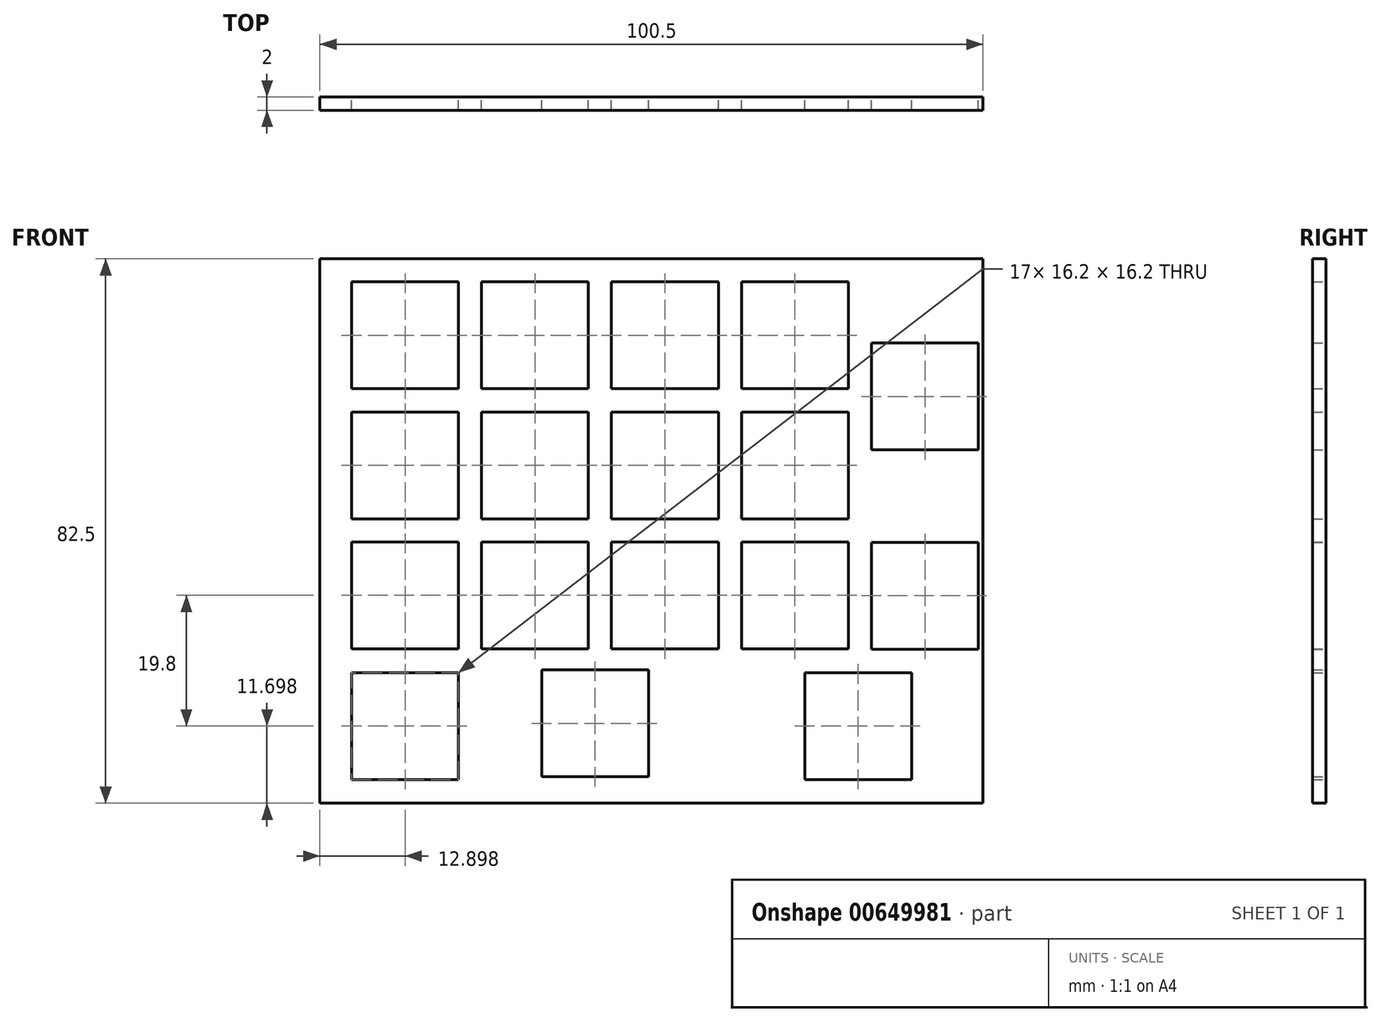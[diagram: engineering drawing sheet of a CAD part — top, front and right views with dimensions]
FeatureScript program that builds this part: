
annotation { "Feature Type Name" : "Feature", "Feature Type Description" : "" }
export const myFeature = defineFeature(function(context is Context, id is Id, definition is map)
    precondition{}
    {
        {
            var Q0;
            Q0=qCreatedBy(makeId("Front.planeOp"),FACE);
            var sketch = newSketch(context, id + "F0", { "sketchPlane" : qUnion([Q0])});
            skLineSegment(sketch, "E0.bottom", {"start": v(-117.36, -39.18) * mm, "end": v(-16.86, -39.18) * mm});
            skLineSegment(sketch, "E0.top", {"start": v(-117.36, 43.32) * mm, "end": v(-16.86, 43.32) * mm});
            skLineSegment(sketch, "E0.left", {"start": v(-117.36, -39.18) * mm, "end": v(-117.36, 43.32) * mm});
            skLineSegment(sketch, "E0.right", {"start": v(-16.86, -39.18) * mm, "end": v(-16.86, 43.32) * mm});
            skPoint(sketch, "E0.middle", {"position": v(-67.11, 2.07) * mm});
            skSolve(sketch);
        }
        {
            var Q0;
            Q0=makeQuery(id+"F0.imprint","IMPRINT",FACE,{"disambiguationData":[TD([[makeQuery(id+"F0.imprint","IMPRINT",EDGE,{"derivedFrom":sQuery(id+"F0.wireOp",EDGE,"E0.bottom")}),1.0]])]});
            extrude(context, id + "F1", {"entities" : qUnion([Q0]), "depth" : 2 * mm, "offsetDistance" : 25 * mm});
        }
        {
            var Q0;
            Q0=qCreatedBy(makeId("Front.planeOp"),FACE);
            var sketch = newSketch(context, id + "F2", { "sketchPlane" : qUnion([Q0])});
            skLineSegment(sketch, "E1.bottom", {"start": v(-96.36, 23.62) * mm, "end": v(-112.56, 23.62) * mm});
            skLineSegment(sketch, "E1.top", {"start": v(-96.36, 39.82) * mm, "end": v(-112.56, 39.82) * mm});
            skLineSegment(sketch, "E1.left", {"start": v(-96.36, 23.62) * mm, "end": v(-96.36, 39.82) * mm});
            skLineSegment(sketch, "E1.right", {"start": v(-112.56, 23.62) * mm, "end": v(-112.56, 39.82) * mm});
            skPoint(sketch, "E1.middle", {"position": v(-104.46, 31.72) * mm});
            skLineSegment(sketch, "E2.bottom", {"start": v(-96.36, 3.92) * mm, "end": v(-112.56, 3.92) * mm});
            skLineSegment(sketch, "E2.top", {"start": v(-96.36, 20.12) * mm, "end": v(-112.56, 20.12) * mm});
            skLineSegment(sketch, "E2.left", {"start": v(-96.36, 3.92) * mm, "end": v(-96.36, 20.12) * mm});
            skLineSegment(sketch, "E2.right", {"start": v(-112.56, 3.92) * mm, "end": v(-112.56, 20.12) * mm});
            skPoint(sketch, "E2.middle", {"position": v(-104.46, 12.02) * mm});
            skLineSegment(sketch, "E3.bottom", {"start": v(-112.56, -15.78) * mm, "end": v(-96.36, -15.78) * mm});
            skLineSegment(sketch, "E3.top", {"start": v(-112.56, 0.42) * mm, "end": v(-96.36, 0.42) * mm});
            skLineSegment(sketch, "E3.left", {"start": v(-112.56, -15.78) * mm, "end": v(-112.56, 0.42) * mm});
            skLineSegment(sketch, "E3.right", {"start": v(-96.36, -15.78) * mm, "end": v(-96.36, 0.42) * mm});
            skPoint(sketch, "E3.middle", {"position": v(-104.46, -7.68) * mm});
            skLineSegment(sketch, "E4.bottom", {"start": v(-112.56, -35.58) * mm, "end": v(-96.36, -35.58) * mm});
            skLineSegment(sketch, "E4.top", {"start": v(-112.56, -19.38) * mm, "end": v(-96.36, -19.38) * mm});
            skLineSegment(sketch, "E4.left", {"start": v(-112.56, -35.58) * mm, "end": v(-112.56, -19.38) * mm});
            skLineSegment(sketch, "E4.right", {"start": v(-96.36, -35.58) * mm, "end": v(-96.36, -19.38) * mm});
            skPoint(sketch, "E4.middle", {"position": v(-104.46, -27.48) * mm});
            skLineSegment(sketch, "E5.bottom", {"start": v(-92.86, 23.62) * mm, "end": v(-76.66, 23.62) * mm});
            skLineSegment(sketch, "E5.top", {"start": v(-92.86, 39.82) * mm, "end": v(-76.66, 39.82) * mm});
            skLineSegment(sketch, "E5.left", {"start": v(-92.86, 23.62) * mm, "end": v(-92.86, 39.82) * mm});
            skLineSegment(sketch, "E5.right", {"start": v(-76.66, 23.62) * mm, "end": v(-76.66, 39.82) * mm});
            skPoint(sketch, "E5.middle", {"position": v(-84.76, 31.72) * mm});
            skLineSegment(sketch, "E6.bottom", {"start": v(-92.86, 3.92) * mm, "end": v(-76.66, 3.92) * mm});
            skLineSegment(sketch, "E6.top", {"start": v(-92.86, 20.12) * mm, "end": v(-76.66, 20.12) * mm});
            skLineSegment(sketch, "E6.left", {"start": v(-92.86, 3.92) * mm, "end": v(-92.86, 20.12) * mm});
            skLineSegment(sketch, "E6.right", {"start": v(-76.66, 3.92) * mm, "end": v(-76.66, 20.12) * mm});
            skPoint(sketch, "E6.middle", {"position": v(-84.76, 12.02) * mm});
            skPoint(sketch, "E6.cornerSnap0", {"position": v(-104.46, 3.92) * mm});
            skLineSegment(sketch, "E7.bottom", {"start": v(-92.86, -15.78) * mm, "end": v(-76.66, -15.78) * mm});
            skLineSegment(sketch, "E7.top", {"start": v(-92.86, 0.42) * mm, "end": v(-76.66, 0.42) * mm});
            skLineSegment(sketch, "E7.left", {"start": v(-92.86, -15.78) * mm, "end": v(-92.86, 0.42) * mm});
            skLineSegment(sketch, "E7.right", {"start": v(-76.66, -15.78) * mm, "end": v(-76.66, 0.42) * mm});
            skPoint(sketch, "E7.middle", {"position": v(-84.76, -7.68) * mm});
            skLineSegment(sketch, "E8.bottom", {"start": v(-73.16, 23.62) * mm, "end": v(-56.96, 23.62) * mm});
            skLineSegment(sketch, "E8.top", {"start": v(-73.16, 39.82) * mm, "end": v(-56.96, 39.82) * mm});
            skLineSegment(sketch, "E8.left", {"start": v(-73.16, 23.62) * mm, "end": v(-73.16, 39.82) * mm});
            skLineSegment(sketch, "E8.right", {"start": v(-56.96, 23.62) * mm, "end": v(-56.96, 39.82) * mm});
            skPoint(sketch, "E8.middle", {"position": v(-65.06, 31.72) * mm});
            skLineSegment(sketch, "E9.bottom", {"start": v(-73.16, 3.92) * mm, "end": v(-56.96, 3.92) * mm});
            skLineSegment(sketch, "E9.top", {"start": v(-73.16, 20.12) * mm, "end": v(-56.96, 20.12) * mm});
            skLineSegment(sketch, "E9.left", {"start": v(-73.16, 3.92) * mm, "end": v(-73.16, 20.12) * mm});
            skLineSegment(sketch, "E9.right", {"start": v(-56.96, 3.92) * mm, "end": v(-56.96, 20.12) * mm});
            skPoint(sketch, "E9.middle", {"position": v(-65.06, 12.02) * mm});
            skLineSegment(sketch, "E10.bottom", {"start": v(-73.16, 0.42) * mm, "end": v(-56.96, 0.42) * mm});
            skLineSegment(sketch, "E10.top", {"start": v(-73.16, -15.78) * mm, "end": v(-56.96, -15.78) * mm});
            skLineSegment(sketch, "E10.left", {"start": v(-73.16, 0.42) * mm, "end": v(-73.16, -15.78) * mm});
            skLineSegment(sketch, "E10.right", {"start": v(-56.96, 0.42) * mm, "end": v(-56.96, -15.78) * mm});
            skPoint(sketch, "E10.middle", {"position": v(-65.06, -7.68) * mm});
            skLineSegment(sketch, "E11.bottom", {"start": v(-53.46, 39.82) * mm, "end": v(-37.26, 39.82) * mm});
            skLineSegment(sketch, "E11.top", {"start": v(-53.46, 23.62) * mm, "end": v(-37.26, 23.62) * mm});
            skLineSegment(sketch, "E11.left", {"start": v(-53.46, 39.82) * mm, "end": v(-53.46, 23.62) * mm});
            skLineSegment(sketch, "E11.right", {"start": v(-37.26, 39.82) * mm, "end": v(-37.26, 23.62) * mm});
            skPoint(sketch, "E11.middle", {"position": v(-45.36, 31.72) * mm});
            skLineSegment(sketch, "E12.bottom", {"start": v(-53.46, 20.12) * mm, "end": v(-37.26, 20.12) * mm});
            skLineSegment(sketch, "E12.top", {"start": v(-53.46, 3.92) * mm, "end": v(-37.26, 3.92) * mm});
            skLineSegment(sketch, "E12.left", {"start": v(-53.46, 20.12) * mm, "end": v(-53.46, 3.92) * mm});
            skLineSegment(sketch, "E12.right", {"start": v(-37.26, 20.12) * mm, "end": v(-37.26, 3.92) * mm});
            skPoint(sketch, "E12.middle", {"position": v(-45.36, 12.02) * mm});
            skLineSegment(sketch, "E13.bottom", {"start": v(-53.46, 0.42) * mm, "end": v(-37.26, 0.42) * mm});
            skLineSegment(sketch, "E13.top", {"start": v(-53.46, -15.78) * mm, "end": v(-37.26, -15.78) * mm});
            skLineSegment(sketch, "E13.left", {"start": v(-53.46, 0.42) * mm, "end": v(-53.46, -15.78) * mm});
            skLineSegment(sketch, "E13.right", {"start": v(-37.26, 0.42) * mm, "end": v(-37.26, -15.78) * mm});
            skPoint(sketch, "E13.middle", {"position": v(-45.36, -7.68) * mm});
            skLineSegment(sketch, "E14.bottom", {"start": v(-67.56, -18.98) * mm, "end": v(-83.76, -18.98) * mm});
            skLineSegment(sketch, "E14.top", {"start": v(-67.56, -35.18) * mm, "end": v(-83.76, -35.18) * mm});
            skLineSegment(sketch, "E14.left", {"start": v(-67.56, -18.98) * mm, "end": v(-67.56, -35.18) * mm});
            skLineSegment(sketch, "E14.right", {"start": v(-83.76, -18.98) * mm, "end": v(-83.76, -35.18) * mm});
            skPoint(sketch, "E14.middle", {"position": v(-75.66, -27.08) * mm});
            skLineSegment(sketch, "E15.bottom", {"start": v(-27.66, -19.38) * mm, "end": v(-43.86, -19.38) * mm});
            skLineSegment(sketch, "E15.top", {"start": v(-27.66, -35.58) * mm, "end": v(-43.86, -35.58) * mm});
            skLineSegment(sketch, "E15.left", {"start": v(-27.66, -19.38) * mm, "end": v(-27.66, -35.58) * mm});
            skLineSegment(sketch, "E15.right", {"start": v(-43.86, -19.38) * mm, "end": v(-43.86, -35.58) * mm});
            skPoint(sketch, "E15.middle", {"position": v(-35.76, -27.48) * mm});
            skLineSegment(sketch, "E16.bottom", {"start": v(-33.76, 0.37) * mm, "end": v(-17.56, 0.37) * mm});
            skLineSegment(sketch, "E16.top", {"start": v(-33.76, -15.83) * mm, "end": v(-17.56, -15.83) * mm});
            skLineSegment(sketch, "E16.left", {"start": v(-33.76, 0.37) * mm, "end": v(-33.76, -15.83) * mm});
            skLineSegment(sketch, "E16.right", {"start": v(-17.56, 0.37) * mm, "end": v(-17.56, -15.83) * mm});
            skPoint(sketch, "E16.middle", {"position": v(-25.66, -7.73) * mm});
            skLineSegment(sketch, "E17.bottom", {"start": v(-33.76, 14.37) * mm, "end": v(-17.56, 14.37) * mm});
            skLineSegment(sketch, "E17.top", {"start": v(-33.76, 30.57) * mm, "end": v(-17.56, 30.57) * mm});
            skLineSegment(sketch, "E17.left", {"start": v(-33.76, 14.37) * mm, "end": v(-33.76, 30.57) * mm});
            skLineSegment(sketch, "E17.right", {"start": v(-17.56, 14.37) * mm, "end": v(-17.56, 30.57) * mm});
            skPoint(sketch, "E17.middle", {"position": v(-25.66, 22.47) * mm});
            skSolve(sketch);
        }
        {
            var Q0;
            Q0 = qSketchRegion(id + "F2", true);
            extrude(context, id + "F3", {"entities" : qUnion([Q0]), "operationType" : NewBodyOperationType.REMOVE, "depth" : 25 * mm, "offsetDistance" : 25 * mm});
        }
    });
